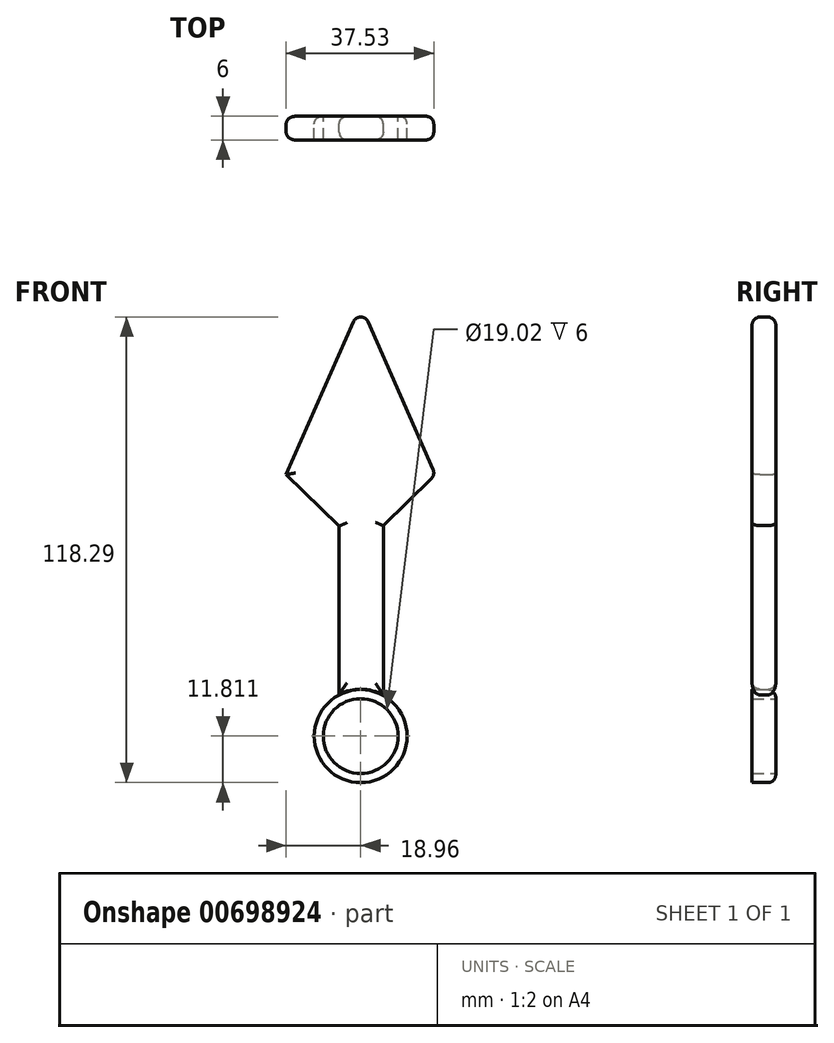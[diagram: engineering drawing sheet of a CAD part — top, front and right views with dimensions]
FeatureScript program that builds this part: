
annotation { "Feature Type Name" : "Feature", "Feature Type Description" : "" }
export const myFeature = defineFeature(function(context is Context, id is Id, definition is map)
    precondition{}
    {
        {
            var Q0;
            Q0=qCreatedBy(makeId("Front.planeOp"),FACE);
            var sketch = newSketch(context, id + "F0", { "sketchPlane" : qUnion([Q0])});
            skLineSegment(sketch, "E0", {"start": v(0, 75.47) * mm, "end": v(-18.96, 32.45) * mm});
            skLineSegment(sketch, "E1", {"start": v(-18.96, 32.45) * mm, "end": v(-5.47, 19.42) * mm});
            skLineSegment(sketch, "E2", {"start": v(-5.47, 19.42) * mm, "end": v(-5.47, 0) * mm});
            skLineSegment(sketch, "E3", {"start": v(0, 75.47) * mm, "end": v(18.96, 32.45) * mm});
            skLineSegment(sketch, "E4", {"start": v(5.74, 0.09) * mm, "end": v(5.74, 19.5) * mm});
            skLineSegment(sketch, "E5", {"start": v(5.74, 19.5) * mm, "end": v(18.96, 32.45) * mm});
            skLineSegment(sketch, "E6", {"start": v(-5.47, 0) * mm, "end": v(-5.47, -23.38) * mm});
            skLineSegment(sketch, "E7", {"start": v(5.74, 0.09) * mm, "end": v(5.74, -23.52) * mm});
            skPoint(sketch, "E8.start.orphan", {"position": v(0, -33.97) * mm});
            skCircle(sketch, "E9", {"center": v(0, -33.97) * mm, "radius": 11.81 * mm});
            skArc(sketch, "E10", {"start": v(5.74, -23.52) * mm, "mid": v(0.15, -22.05) * mm, "end": v(-5.47, -23.38) * mm});
            skCircle(sketch, "E11", {"center": v(0, -33.97) * mm, "radius": 9.5 * mm});
            skSolve(sketch);
        }
        {
            var Q0;
            Q0=makeQuery(id+"F0.imprint","IMPRINT",FACE,{"disambiguationData":[TD([[makeQuery(id+"F0.imprint","IMPRINT",EDGE,{"derivedFrom":sQuery(id+"F0.wireOp",EDGE,"E0")}),1.0]])]});
            extrude(context, id + "F1", {"entities" : qUnion([Q0]), "depth" : 5 * mm, "offsetDistance" : 25 * mm});
        }
        {
            var Q0;
            Q0 = qSketchRegion(id + "F0", true);
            extrude(context, id + "F2", {"entities" : qUnion([Q0]), "operationType" : NewBodyOperationType.ADD, "depth" : 6 * mm, "offsetDistance" : 25 * mm});
        }
        {
            var Q0;
            Q0=makeQuery(id+"F2.opExtrude","CAP_FACE",FACE,{"disambiguationData":[OSD([sQuery(id+"F0.wireOp",EDGE,"E0"),sQuery(id+"F0.wireOp",EDGE,"E1"),sQuery(id+"F0.wireOp",EDGE,"E2"),sQuery(id+"F0.wireOp",EDGE,"E3"),sQuery(id+"F0.wireOp",EDGE,"E4"),sQuery(id+"F0.wireOp",EDGE,"E5"),sQuery(id+"F0.wireOp",EDGE,"E6"),sQuery(id+"F0.wireOp",EDGE,"E7"),sQuery(id+"F0.wireOp",EDGE,"E10")])],"isStart":false});
            var Q1;
            {var subQ0=sQuery(id+"F0.wireOp",EDGE,"E3");Q1=makeQuery(id+"F2.boolean.opBoolean","MERGE",FACE,{"derivedFrom":[makeQuery(id+"F1.opExtrude","SWEPT_FACE",FACE,{"disambiguationData":[OSD([subQ0])]}),makeQuery(id+"F2.opExtrude","SWEPT_FACE",FACE,{"disambiguationData":[OSD([subQ0])]})]});}
            var Q2;
            Q2=makeQuery(id+"F1.opExtrude","CAP_EDGE",EDGE,{"disambiguationData":[OSD([sQuery(id+"F0.wireOp",EDGE,"E3")])],"isStart":true});
            var Q3;
            Q3=makeQuery(id+"F1.opExtrude","CAP_EDGE",EDGE,{"disambiguationData":[OSD([sQuery(id+"F0.wireOp",EDGE,"E5")])],"isStart":true});
            var Q4;
            Q4=makeQuery(id+"F1.opExtrude","CAP_EDGE",EDGE,{"disambiguationData":[OSD([sQuery(id+"F0.wireOp",EDGE,"E1")])],"isStart":true});
            var Q5;
            Q5=makeQuery(id+"F1.opExtrude","CAP_EDGE",EDGE,{"disambiguationData":[OSD([sQuery(id+"F0.wireOp",EDGE,"E2"),sQuery(id+"F0.wireOp",EDGE,"E6")])],"isStart":true});
            var Q6;
            Q6=makeQuery(id+"F1.opExtrude","CAP_EDGE",EDGE,{"disambiguationData":[OSD([sQuery(id+"F0.wireOp",EDGE,"E4"),sQuery(id+"F0.wireOp",EDGE,"E7")])],"isStart":true});
            var Q7;
            Q7=makeQuery(id+"F2.opExtrude","CAP_EDGE",EDGE,{"disambiguationData":[OSD([sQuery(id+"F0.wireOp",EDGE,"E9")])],"isStart":true});
            var Q8;
            Q8=makeQuery(id+"F1.opExtrude","CAP_FACE",FACE,{"disambiguationData":[OSD([sQuery(id+"F0.wireOp",EDGE,"E0"),sQuery(id+"F0.wireOp",EDGE,"E1"),sQuery(id+"F0.wireOp",EDGE,"E2"),sQuery(id+"F0.wireOp",EDGE,"E3"),sQuery(id+"F0.wireOp",EDGE,"E4"),sQuery(id+"F0.wireOp",EDGE,"E5"),sQuery(id+"F0.wireOp",EDGE,"E6"),sQuery(id+"F0.wireOp",EDGE,"E7"),sQuery(id+"F0.wireOp",EDGE,"E10")])],"isStart":true});
            fillet(context, id + "F3", {"entities" : qUnion([Q0, Q1, Q2, Q3, Q4, Q5, Q6, Q7, Q8]), "radius" : 2 * mm, "tangentPropagation" : true, "allowEdgeOverflow" : false});
        }
        {
            var Q0;
            Q0=makeQuery(id+"F2.opExtrude","CAP_EDGE",EDGE,{"disambiguationData":[OSD([sQuery(id+"F0.wireOp",EDGE,"E9")])],"isStart":false});
            var Q1;
            {var subQ0=sQuery(id+"F0.wireOp",EDGE,"E10");Q1=makeQuery(id+"F3.opFillet","BLEND_EDGE",EDGE,{"blendedFrom":[makeQuery(id+"F2.opExtrude","CAP_EDGE",EDGE,{"disambiguationData":[OSD([subQ0])],"isStart":false}),makeQuery(id+"F2.opExtrude","CAP_FACE",FACE,{"disambiguationData":[OSD([sQuery(id+"F0.wireOp",EDGE,"E0"),sQuery(id+"F0.wireOp",EDGE,"E1"),sQuery(id+"F0.wireOp",EDGE,"E2"),sQuery(id+"F0.wireOp",EDGE,"E3"),sQuery(id+"F0.wireOp",EDGE,"E4"),sQuery(id+"F0.wireOp",EDGE,"E5"),sQuery(id+"F0.wireOp",EDGE,"E6"),sQuery(id+"F0.wireOp",EDGE,"E7"),subQ0])],"isStart":false})],"blendedInto":[makeQuery(id+"F2.opExtrude","CAP_FACE",FACE,{"disambiguationData":[OSD([sQuery(id+"F0.wireOp",EDGE,"E0"),sQuery(id+"F0.wireOp",EDGE,"E1"),sQuery(id+"F0.wireOp",EDGE,"E2"),sQuery(id+"F0.wireOp",EDGE,"E3"),sQuery(id+"F0.wireOp",EDGE,"E4"),sQuery(id+"F0.wireOp",EDGE,"E5"),sQuery(id+"F0.wireOp",EDGE,"E6"),sQuery(id+"F0.wireOp",EDGE,"E7"),subQ0])],"isStart":false})]});}
            fillet(context, id + "F4", {"entities" : qUnion([Q0, Q1]), "radius" : 5 * mm, "tangentPropagation" : true, "allowEdgeOverflow" : false});
        }
    });
